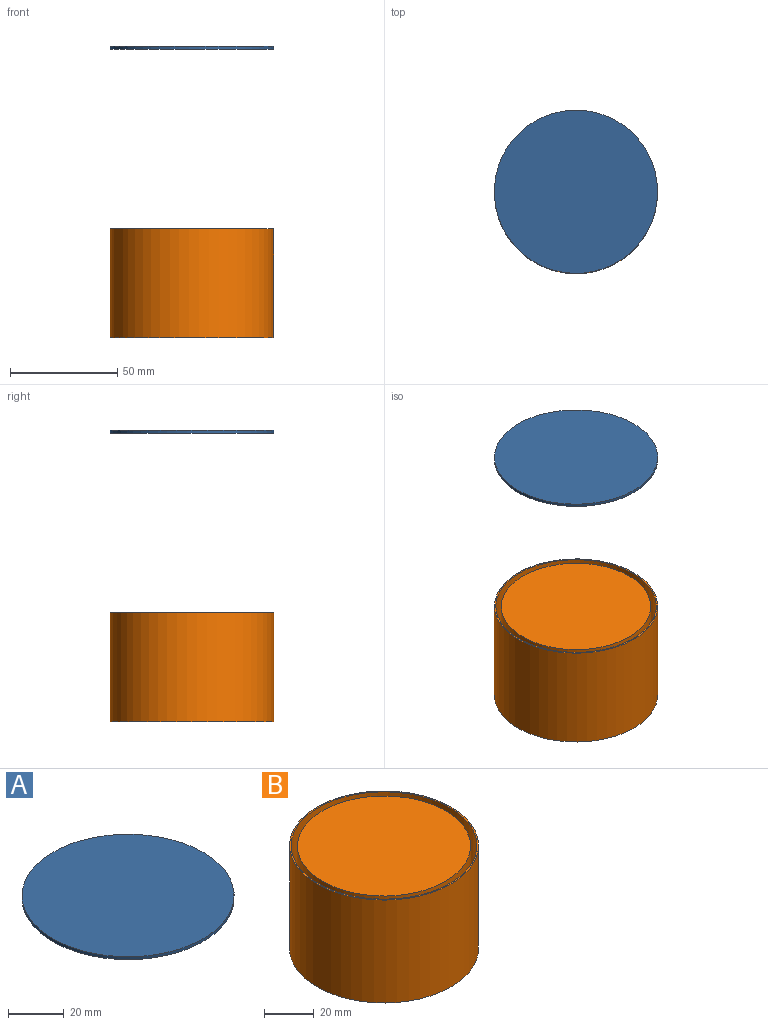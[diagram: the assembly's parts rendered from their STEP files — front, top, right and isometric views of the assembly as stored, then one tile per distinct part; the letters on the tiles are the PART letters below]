
ASSEMBLY  parts=2 mates=1
PART A: 3 faces, bbox 76.2x76.2x1.3 mm
  f0: cylinder r=38.1mm len=76.2mm, axis (0,0,-1), area 304mm2, adj f1,f2
  f1: plane 76.2x76.2mm, normal (0,0,1), area 4560.4mm2, adj f0
  f2: plane 76.2x76.2mm, normal (0,0,-1), area 4560.4mm2, adj f0
PART B: 7 faces, bbox 76.2x76.2x50.8 mm
  f0: cylinder r=38.1mm len=76.2mm, axis (0,0,-1), area 12161mm2, adj f1,f2
  f1: plane 76.2x76.2mm, normal (0,0,1), area 150.7mm2, adj f0,f3
  f2: plane 76.2x76.2mm, normal (0,0,-1), area 4560.4mm2, adj f0
  f3: cylinder r=37.46mm len=74.93mm, axis (0,0,1), area 11898.5mm2, adj f1,f5
  f4: cylinder r=34.92mm len=69.85mm, axis (0,0,1), area 11036.1mm2, adj f5,f6
  f5: plane 74.93x74.93mm, normal (0,0,1), area 577.6mm2, adj f3,f4
  f6: plane 69.85x69.85mm, normal (0,0,1), area 3832mm2, adj f4
PLACE A t=(-66.61,-22.88,72.64)mm
PLACE B t=(-66.61,-22.88,-62.06)mm
MATE cylindrical A.f0 <-> B.f4  axis (0,0,1) through (-66.61,-22.88,73.91)mm
